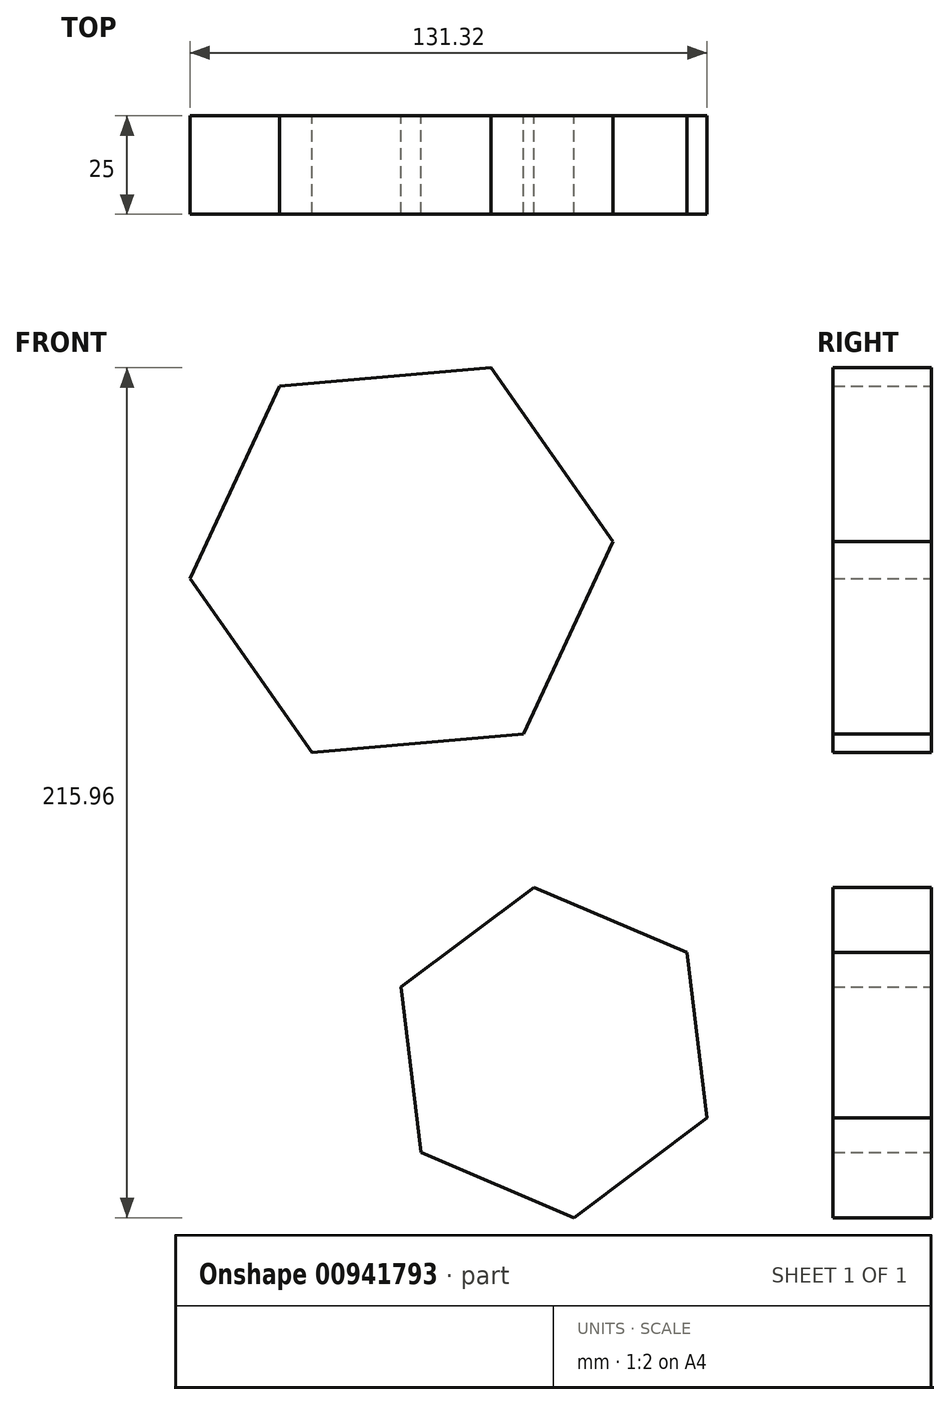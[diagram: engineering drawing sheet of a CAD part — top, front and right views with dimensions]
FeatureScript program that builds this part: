
annotation { "Feature Type Name" : "Feature", "Feature Type Description" : "" }
export const myFeature = defineFeature(function(context is Context, id is Id, definition is map)
    precondition{}
    {
        {
            var Q0;
            Q0=qCreatedBy(makeId("Front.planeOp"),FACE);
            var sketch = newSketch(context, id + "F0", { "sketchPlane" : qUnion([Q0])});
            skCircle(sketch, "E0.cCircle", {"center": v(110.37, 54.42) * mm, "radius": 46.7 * mm, "construction": true});
            skLineSegment(sketch, "E0.0", {"start": v(141.3, 10.25) * mm, "end": v(87.59, 5.54) * mm});
            skLineSegment(sketch, "E0.1", {"start": v(87.59, 5.54) * mm, "end": v(56.65, 49.71) * mm});
            skLineSegment(sketch, "E0.2", {"start": v(56.65, 49.71) * mm, "end": v(79.44, 98.59) * mm});
            skLineSegment(sketch, "E0.3", {"start": v(79.44, 98.59) * mm, "end": v(133.16, 103.3) * mm});
            skLineSegment(sketch, "E0.4", {"start": v(133.16, 103.3) * mm, "end": v(164.1, 59.12) * mm});
            skLineSegment(sketch, "E0.5", {"start": v(164.1, 59.12) * mm, "end": v(141.3, 10.25) * mm});
            skPoint(sketch, "E0.0.midPoint", {"position": v(114.45, 7.9) * mm});
            skCircle(sketch, "E1.cCircle", {"center": v(149.09, -70.7) * mm, "radius": 36.61 * mm, "construction": true});
            skLineSegment(sketch, "E1.0", {"start": v(154.15, -112.67) * mm, "end": v(115.27, -96.06) * mm});
            skLineSegment(sketch, "E1.1", {"start": v(115.27, -96.06) * mm, "end": v(110.21, -54.1) * mm});
            skLineSegment(sketch, "E1.2", {"start": v(110.21, -54.1) * mm, "end": v(144.03, -28.72) * mm});
            skLineSegment(sketch, "E1.3", {"start": v(144.03, -28.72) * mm, "end": v(182.9, -45.33) * mm});
            skLineSegment(sketch, "E1.4", {"start": v(182.9, -45.33) * mm, "end": v(187.97, -87.3) * mm});
            skLineSegment(sketch, "E1.5", {"start": v(187.97, -87.3) * mm, "end": v(154.15, -112.67) * mm});
            skPoint(sketch, "E1.0.midPoint", {"position": v(134.7, -104.37) * mm});
            skSolve(sketch);
        }
        {
            var Q0;
            Q0 = qSketchRegion(id + "F0", true);
            extrude(context, id + "F1", {"entities" : qUnion([Q0]), "depth" : 25 * mm, "offsetDistance" : 25 * mm});
        }
    });
